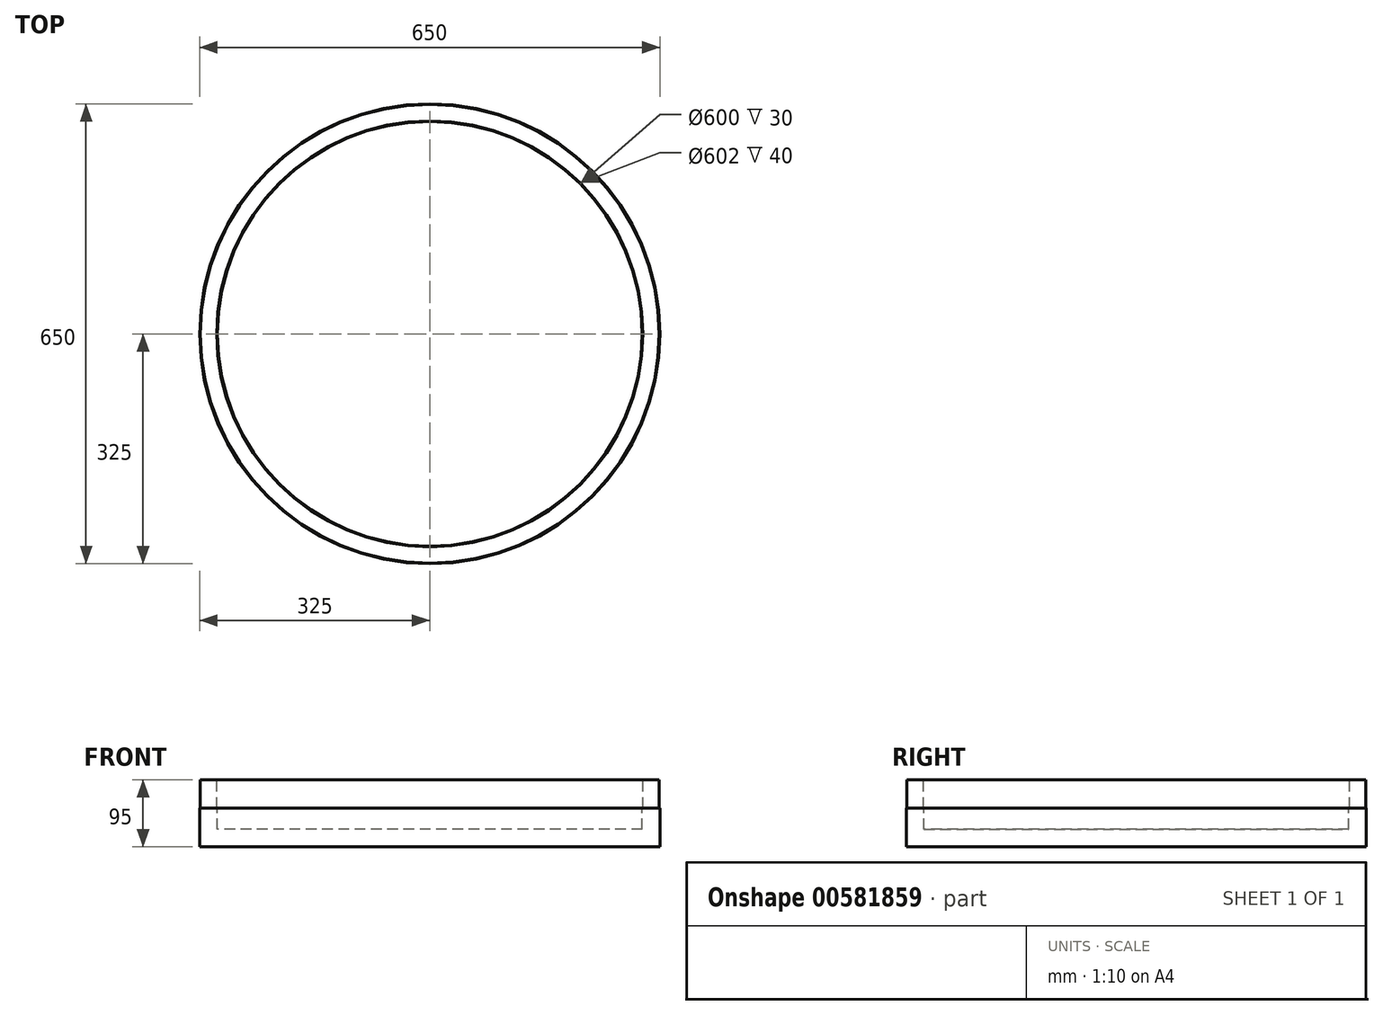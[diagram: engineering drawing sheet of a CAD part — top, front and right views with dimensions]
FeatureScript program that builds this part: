
annotation { "Feature Type Name" : "Feature", "Feature Type Description" : "" }
export const myFeature = defineFeature(function(context is Context, id is Id, definition is map)
    precondition{}
    {
        {
            var Q0;
            Q0=qCreatedBy(makeId("Front.planeOp"),FACE);
            var sketch = newSketch(context, id + "F0", { "sketchPlane" : qUnion([Q0])});
            skLineSegment(sketch, "E0", {"start": v(0, 136.7) * mm, "end": v(0, 0) * mm, "construction": true});
            skLineSegment(sketch, "E1", {"start": v(0, 0) * mm, "end": v(-325, 0) * mm});
            skLineSegment(sketch, "E2", {"start": v(-325, 0) * mm, "end": v(-325, 55) * mm});
            skLineSegment(sketch, "E3", {"start": v(-325, 55) * mm, "end": v(-324, 55) * mm});
            skLineSegment(sketch, "E4", {"start": v(-324, 55) * mm, "end": v(-324, 95) * mm});
            skLineSegment(sketch, "E5", {"start": v(-324, 95) * mm, "end": v(-301, 95) * mm});
            skLineSegment(sketch, "E6", {"start": v(-301, 95) * mm, "end": v(-301, 55) * mm});
            skLineSegment(sketch, "E7", {"start": v(-301, 55) * mm, "end": v(-300, 55) * mm});
            skLineSegment(sketch, "E8", {"start": v(-300, 55) * mm, "end": v(-300, 25) * mm});
            skLineSegment(sketch, "E9", {"start": v(-300, 25) * mm, "end": v(0, 25) * mm});
            skLineSegment(sketch, "E10", {"start": v(0, 25) * mm, "end": v(0, 0) * mm});
            skSolve(sketch);
        }
        {
            var Q0;
            Q0=qSketchRegion(id+"F0",true);
            var Q1;
            Q1=sQuery(id+"F0.wireOp",EDGE,"E0");
            revolve(context, id + "F1", {"surfaceOperationType" : NewSurfaceOperationType.NEW, "entities" : qUnion([Q0]), "axis" : qUnion([Q1]), "revolveType" : RevolveType.FULL});
        }
    });
